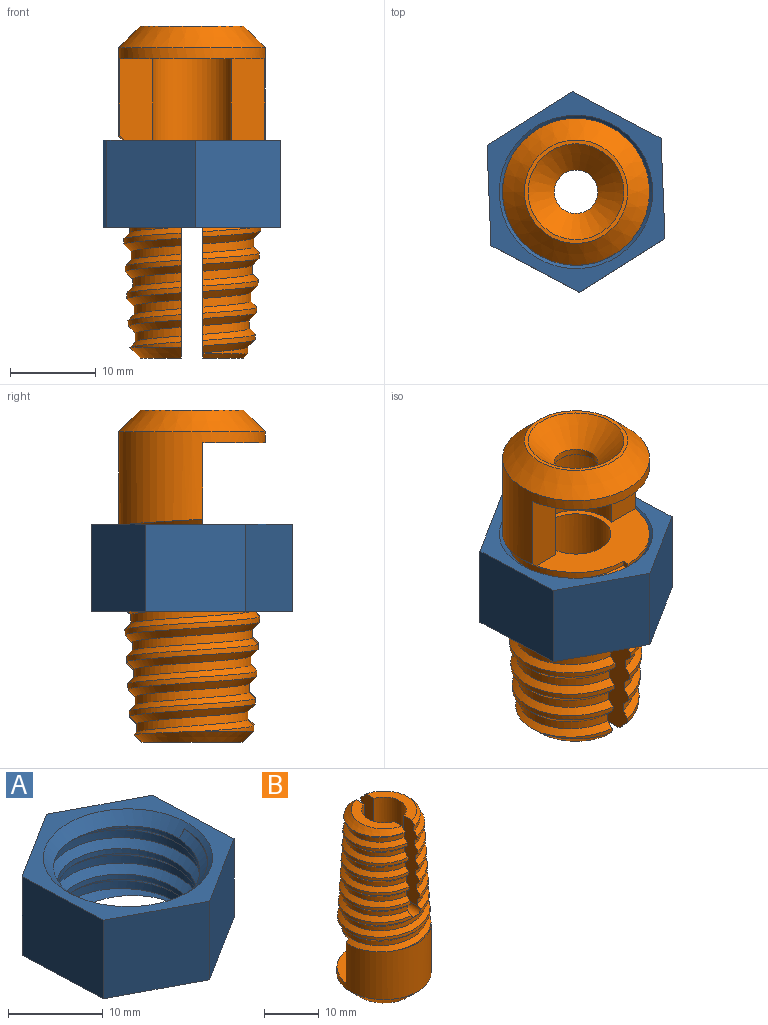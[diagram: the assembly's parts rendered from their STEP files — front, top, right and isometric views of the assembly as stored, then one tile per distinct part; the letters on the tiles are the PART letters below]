
ASSEMBLY  parts=2 mates=1
PART A: 15 faces, bbox 20.8x23.5x12 mm
  f0: cone r=8.95mm half-angle=46.5deg, axis (0,0,1), area 65.7mm2, adj f7,f9,f12,f13,f14
  f1: plane 11.72x10.16mm, normal (1,0.04,0), area 119.2mm2, adj f2,f6,f7,f8
  f2: plane 10.38x10.16mm, normal (0.47,0.88,0), area 119.2mm2, adj f1,f3,f7,f8
  f3: plane 10.16x9.92mm, normal (-0.53,0.85,0), area 119.2mm2, adj f2,f4,f7,f8
  f4: plane 11.72x10.16mm, normal (-1,-0.04,0), area 119.2mm2, adj f3,f5,f7,f8
  f5: plane 10.38x10.16mm, normal (-0.47,-0.88,0), area 119.2mm2, adj f4,f6,f7,f8
  f6: plane 10.16x9.92mm, normal (0.53,-0.85,0), area 119.2mm2, adj f1,f5,f7,f8
  f7: plane 23.45x20.77mm, normal (0,0,1), area 105.9mm2, adj f0,f1,f2,f3,f4,f5,f6
  f8: plane 23.46x20.78mm, normal (0,0,-1), area 186.4mm2, adj f1,f2,f3,f4,f5,f6,f9,f10
  f9: cone r=6.35mm half-angle=3deg, axis (0,0,1), area 91.8mm2, adj f0,f8,f10,f11,f13,f14
  f10: plane 1.21x0.72mm, normal (0.95,0.31,0), area 0.6mm2, adj f8,f9,f12,f14
  f11: bspline ~16.82x16.81mm, area 167.6mm2, adj f8,f9,f12,f13
  f12: bspline ~16.82x16.81mm, area 156.4mm2, adj f0,f8,f10,f11,f13,f14
  f13: plane 0.86x0.83mm, normal (0,-1,0), area 0mm2, adj f0,f9,f11,f12
  f14: bspline ~16.52x16.49mm, area 128mm2, adj f0,f9,f10,f12
PART B: 73 faces, bbox 17.8x17.8x39.4 mm
  f0: cone r=7.24mm half-angle=3deg, axis (0,0,-1), area 76.9mm2, adj f20,f50,f55,f56,f65,f71
  f1: cone r=7.24mm half-angle=3deg, axis (0,0,-1), area 14.3mm2, adj f19,f44,f68,f69
  f2: cone r=7.24mm half-angle=3deg, axis (0,0,-1), area 14mm2, adj f18,f43,f68,f69
  f3: cone r=7.24mm half-angle=3deg, axis (0,0,-1), area 13.7mm2, adj f17,f42,f68,f69
  f4: cone r=7.24mm half-angle=3deg, axis (0,0,-1), area 13.4mm2, adj f16,f41,f68,f69
  f5: cone r=7.24mm half-angle=3deg, axis (0,0,-1), area 13.1mm2, adj f15,f40,f68,f69
  f6: cone r=7.24mm half-angle=3deg, axis (0,0,-1), area 2.7mm2, adj f12,f39,f69
  f7: cone r=7.24mm half-angle=3deg, axis (0,0,-1), area 12.9mm2, adj f26,f45,f67,f70
  f8: cone r=7.24mm half-angle=3deg, axis (0,0,-1), area 13.2mm2, adj f21,f46,f67,f70
  f9: cone r=7.24mm half-angle=3deg, axis (0,0,-1), area 13.6mm2, adj f22,f47,f67,f70
  f10: cone r=7.24mm half-angle=3deg, axis (0,0,-1), area 13.9mm2, adj f23,f48,f67,f70
  f11: cone r=7.24mm half-angle=3deg, axis (0,0,-1), area 14.2mm2, adj f24,f49,f67,f70
  f12: cone r=5.97mm half-angle=46.5deg, axis (0,0,-1), area 30.3mm2, adj f6,f14,f39,f68,f69
  f13: cylinder r=4.06mm len=25.4mm, axis (0,0,-1), area 548.3mm2, adj f14,f56,f57,f67,f68,f69,f70,f71
  f14: plane 11.67x4.7mm, normal (0,0,1), area 25.2mm2, adj f12,f13,f68,f69
  f15: bspline ~15.56x10.87mm, area 23mm2, adj f5,f27,f68,f69
  f16: bspline ~15.89x12.34mm, area 23.6mm2, adj f4,f28,f68,f69
  f17: bspline ~16.22x12.66mm, area 24.2mm2, adj f3,f29,f68,f69
  f18: bspline ~16.59x11.54mm, area 24.9mm2, adj f2,f30,f68,f69
  f19: bspline ~16.79x11.02mm, area 25.5mm2, adj f1,f31,f68,f69
  f20: bspline ~17.77x17.74mm, area 133.7mm2, adj f0,f32,f55,f56,f63,f66,f68,f71
  f21: bspline ~15.75x12.57mm, area 23.3mm2, adj f8,f34,f67,f70
  f22: bspline ~16.03x12.13mm, area 23.9mm2, adj f9,f35,f67,f70
  f23: bspline ~16.43x13.18mm, area 24.6mm2, adj f10,f36,f67,f70
  f24: bspline ~16.71x11.3mm, area 25.2mm2, adj f11,f37,f67,f70
  f25: bspline ~16.82x10.71mm, area 25.8mm2, adj f38,f52,f67,f70,f71
  f26: bspline ~15.22x10.41mm, area 22.7mm2, adj f7,f33,f67,f70
  f27: bspline ~13.49x9.43mm, area 18.5mm2, adj f15,f39,f68,f69
  f28: bspline ~13.82x10.73mm, area 19mm2, adj f16,f40,f68,f69
  f29: bspline ~14.15x11.05mm, area 19.5mm2, adj f17,f41,f68,f69
  f30: bspline ~14.51x10.09mm, area 20.1mm2, adj f18,f42,f68,f69
  f31: bspline ~14.73x9.67mm, area 20.6mm2, adj f19,f43,f68,f69
  f32: bspline ~14.94x9.53mm, area 21.5mm2, adj f20,f44,f68,f72
  f33: bspline ~13.17x9.01mm, area 12.8mm2, adj f26,f51,f53,f67,f70
  f34: bspline ~13.67x10.91mm, area 18.7mm2, adj f21,f45,f67,f70
  f35: bspline ~13.96x10.57mm, area 19.3mm2, adj f22,f46,f67,f70
  f36: bspline ~14.35x11.52mm, area 19.8mm2, adj f23,f47,f67,f70
  f37: bspline ~14.64x9.9mm, area 20.3mm2, adj f24,f48,f67,f70
  f38: bspline ~14.78x9.4mm, area 20.9mm2, adj f25,f49,f67,f70
  f39: bspline ~15.56x10.87mm, area 16mm2, adj f6,f12,f27,f68,f69
  f40: bspline ~15.89x12.34mm, area 19.6mm2, adj f5,f28,f68,f69
  f41: bspline ~16.22x12.66mm, area 20.2mm2, adj f4,f29,f68,f69
  f42: bspline ~16.59x11.54mm, area 20.7mm2, adj f3,f30,f68,f69
  f43: bspline ~16.79x11.02mm, area 21.2mm2, adj f2,f31,f68,f69
  f44: bspline ~16.98x10.83mm, area 21.7mm2, adj f1,f32,f68,f69,f72
  f45: bspline ~15.75x12.57mm, area 19.4mm2, adj f7,f34,f67,f70
  f46: bspline ~16.03x12.13mm, area 19.9mm2, adj f8,f35,f67,f70
  f47: bspline ~16.43x13.18mm, area 20.4mm2, adj f9,f36,f67,f70
  f48: bspline ~16.71x11.3mm, area 20.9mm2, adj f10,f37,f67,f70
  f49: bspline ~16.82x10.71mm, area 21.5mm2, adj f11,f38,f67,f70
  f50: bspline ~17.77x17.74mm, area 98mm2, adj f0,f52,f65,f66,f70,f71,f72
  f51: bspline ~10.21x6.2mm, area 0.9mm2, adj f33,f53,f67
  f52: cone r=7.24mm half-angle=3deg, axis (0,0,-1), area 14.7mm2, adj f25,f50,f70,f71
  f53: cone r=5.97mm half-angle=46.5deg, axis (0,0,-1), area 13.8mm2, adj f33,f51,f57,f67,f70
  f54: cylinder r=4.76mm len=9.53mm, axis (0,0,-1), area 167mm2, adj f56,f58,f62,f63
  f55: cylinder r=8.57mm len=17.15mm, axis (0,0,-1), area 346.1mm2, adj f0,f20,f58,f62,f63,f64
  f56: plane 16.4x13.37mm, normal (0,0,-1), area 80.7mm2, adj f0,f13,f20,f54,f62,f63,f65,f66
  f57: plane 11.67x4.7mm, normal (0,0,1), area 25.2mm2, adj f13,f53,f67,f70
  f58: plane 16.96x13.34mm, normal (0,0,1), area 121.1mm2, adj f54,f55,f59,f62,f63
  f59: cylinder r=2.54mm len=5.08mm, axis (0,0,1), area 12.2mm2, adj f58,f61
  f60: plane 12.07x12.07mm, normal (0,0,-1), area 16.2mm2, adj f61,f64
  f61: cone r=2.54mm half-angle=45deg, axis (0,0,-1), area 110.1mm2, adj f59,f60
  f62: plane 9.53x3.89mm, normal (0,1,0), area 37mm2, adj f54,f55,f56,f58
  f63: plane 9.53x3.89mm, normal (0,1,0), area 36.9mm2, adj f20,f54,f55,f56,f58
  f64: cone r=8.57mm half-angle=45deg, axis (0,0,1), area 164.8mm2, adj f55,f60
  f65: plane 1.21x0.76mm, normal (-1,0,0), area 0.6mm2, adj f0,f50,f56,f66
  f66: bspline ~15.71x15.68mm, area 94.7mm2, adj f20,f50,f56,f65,f72
  f67: plane 18.43x4.14mm, normal (-1,0,0), area 60.4mm2, adj f7,f8,f9,f10,f11,f13,f21,f22
  f68: plane 18.43x4.15mm, normal (1,0,0), area 60.4mm2, adj f1,f2,f3,f4,f5,f12,f13,f14
  f69: plane 18.44x4.24mm, normal (1,0,0), area 61.2mm2, adj f1,f2,f3,f4,f5,f6,f12,f13
  f70: plane 18.42x4.23mm, normal (-1,0,0), area 61.2mm2, adj f7,f8,f9,f10,f11,f13,f21,f22
  f71: cylinder r=1.27mm len=4.37mm, axis (0,-1,0), area 16.5mm2, adj f0,f13,f20,f25,f50,f52,f67,f68
  f72: cylinder r=1.27mm len=3.75mm, axis (0,1,0), area 13.9mm2, adj f13,f20,f32,f44,f50,f66,f69,f70
PLACE A t=(1.69,13.94,11.41)mm
PLACE B rot(axis=(1,0,0),180deg) t=(1.69,13.94,31.1)mm
MATE fastened B.f13 <-> A.f0  axis (0,0,1) through (1.69,13.94,21.57)mm
